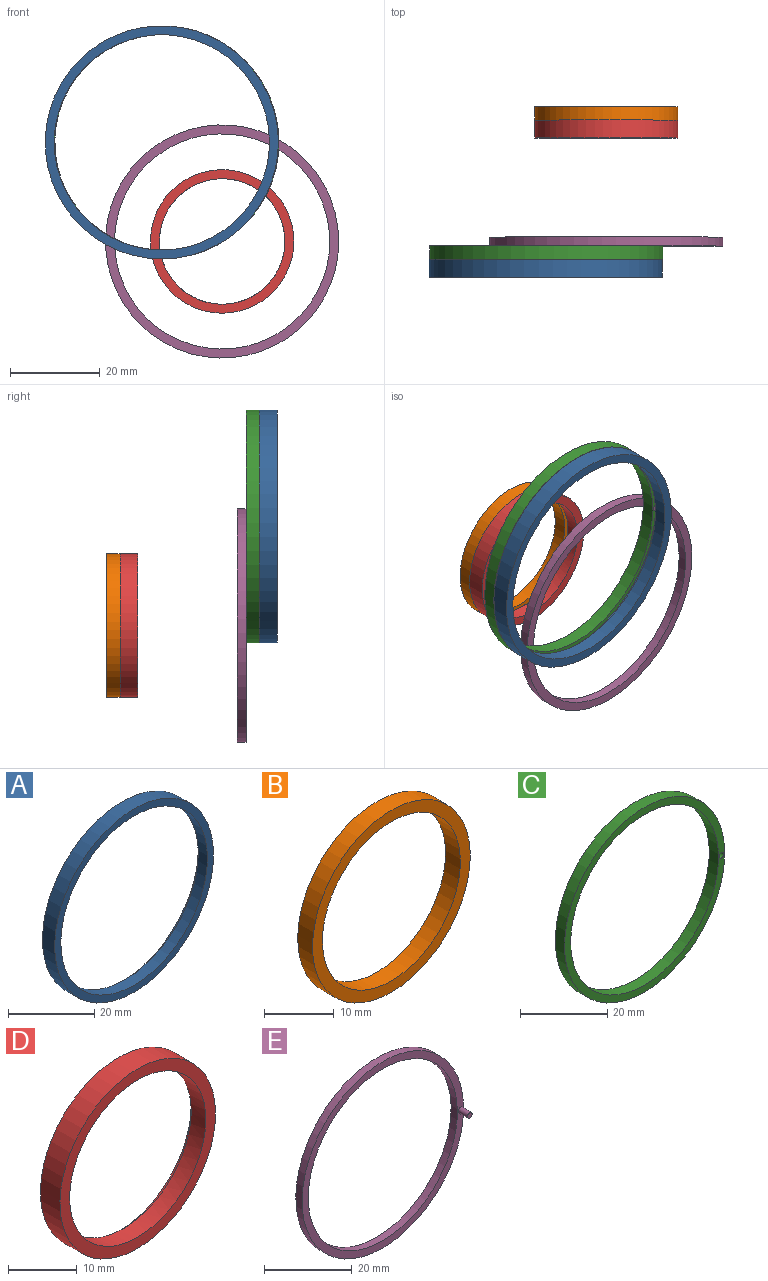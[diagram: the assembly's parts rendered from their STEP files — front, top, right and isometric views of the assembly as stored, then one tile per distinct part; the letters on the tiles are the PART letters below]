
ASSEMBLY  parts=5 mates=4
PART A: 6 faces, bbox 52x4x52 mm
  f0: cylinder r=24mm len=48mm, axis (0,1,0), area 452.4mm2, adj f2,f4
  f1: cylinder r=26mm len=52mm, axis (0,1,0), area 653.5mm2, adj f2,f5
  f2: plane 52x52mm, normal (0,-1,0), area 314.2mm2, adj f0,f1
  f3: cylinder r=25mm len=50mm, axis (0,-1,0), area 157.1mm2, adj f4,f5
  f4: plane 50x50mm, normal (0,1,0), area 153.9mm2, adj f0,f3
  f5: plane 52x52mm, normal (0,1,0), area 160.2mm2, adj f1,f3
PART B: 4 faces, bbox 32x3x32 mm
  f0: cylinder r=14mm len=28mm, axis (0,1,0), area 263.9mm2, adj f2,f3
  f1: cylinder r=16mm len=32mm, axis (0,1,0), area 301.6mm2, adj f2,f3
  f2: plane 32x32mm, normal (0,-1,0), area 188.5mm2, adj f0,f1
  f3: plane 32x32mm, normal (0,1,0), area 188.5mm2, adj f0,f1
PART C: 5 faces, bbox 52x3x52 mm
  f0: cylinder r=24mm len=48mm, axis (0,1,0), area 452.4mm2, adj f3,f4
  f1: cylinder r=0.75mm len=3mm, axis (0,1,0), area 14.1mm2, adj f3,f4
  f2: cylinder r=26mm len=52mm, axis (0,1,0), area 490.1mm2, adj f3,f4
  f3: plane 52x52mm, normal (0,-1,0), area 312.4mm2, adj f0,f1,f2
  f4: plane 52x52mm, normal (0,1,0), area 312.4mm2, adj f0,f1,f2
PART D: 6 faces, bbox 32x4x32 mm
  f0: cylinder r=14mm len=28mm, axis (0,1,0), area 263.9mm2, adj f2,f4
  f1: cylinder r=16mm len=32mm, axis (0,1,0), area 402.1mm2, adj f2,f5
  f2: plane 32x32mm, normal (0,-1,0), area 188.5mm2, adj f0,f1
  f3: cylinder r=15mm len=30mm, axis (0,1,0), area 94.2mm2, adj f4,f5
  f4: plane 30x30mm, normal (0,1,0), area 91.1mm2, adj f0,f3
  f5: plane 32x32mm, normal (0,1,0), area 97.4mm2, adj f1,f3
PART E: 6 faces, bbox 52x5x52 mm
  f0: cylinder r=0.75mm len=3mm, axis (0,1,0), area 14.1mm2, adj f1,f4
  f1: plane 1.5x1.5mm, normal (0,-1,0), area 1.8mm2, adj f0
  f2: cylinder r=24mm len=48mm, axis (0,1,0), area 301.6mm2, adj f4,f5
  f3: cylinder r=26mm len=52mm, axis (0,1,0), area 326.7mm2, adj f4,f5
  f4: plane 52x52mm, normal (0,-1,0), area 312.4mm2, adj f0,f2,f3
  f5: plane 52x52mm, normal (0,1,0), area 314.2mm2, adj f2,f3
PLACE A t=(-54.23,-48.68,40.88)mm fixed
PLACE B rot(axis=(0,-1,0),62.1deg) t=(-40.77,-17.58,18.78)mm
PLACE C t=(-54.09,-48.68,40.88)mm
PLACE D rot(axis=(0,-1,0),62.1deg) t=(-40.77,-17.58,18.78)mm
PLACE E rot(axis=(0,-1,0),62.1deg) t=(-40.77,-46.68,18.78)mm
MATE revolute E.f0 <-> C.f1  axis (0,-1,0) through (-29.08,-51.68,40.88)mm
MATE slider D.f1 <-> E.f3  axis (0,-1,0) through (-40.77,-24.58,18.78)mm
MATE fastened B.f1 <-> D.f1  axis (0,-1,0) through (-40.77,-20.58,18.78)mm
MATE fastened A.f1 <-> C.f3  axis (0,1,0) through (-54.23,-51.68,40.88)mm
